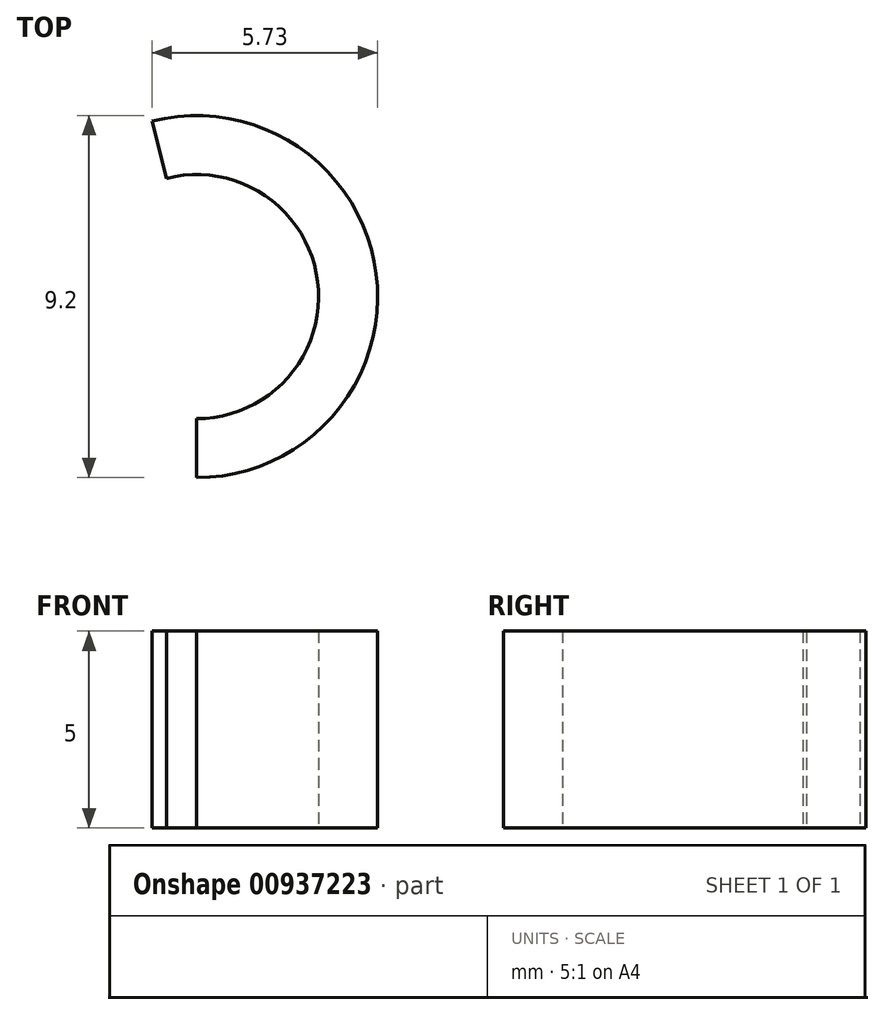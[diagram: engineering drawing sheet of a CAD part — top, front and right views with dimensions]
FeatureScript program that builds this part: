
annotation { "Feature Type Name" : "Feature", "Feature Type Description" : "" }
export const myFeature = defineFeature(function(context is Context, id is Id, definition is map)
    precondition{}
    {
        {
            var Q0;
            Q0=qCreatedBy(makeId("Top.planeOp"),FACE);
            var sketch = newSketch(context, id + "F0", { "sketchPlane" : qUnion([Q0])});
            skCircle(sketch, "E0", {"center": v(0, 0) * mm, "radius": 4.6 * mm});
            skCircle(sketch, "E1", {"center": v(0, 0) * mm, "radius": 3.1 * mm});
            skSolve(sketch);
        }
        {
            var Q0;
            Q0 = qSketchRegion(id + "F0", true);
            extrude(context, id + "F1", {"entities" : qUnion([Q0]), "depth" : 5 * mm, "offsetDistance" : 25 * mm});
        }
        {
            var Q0;
            Q0=qCreatedBy(makeId("Top.planeOp"),FACE);
            var sketch = newSketch(context, id + "F2", { "sketchPlane" : qUnion([Q0])});
            skLineSegment(sketch, "E2", {"start": v(-2.57, 10.12) * mm, "end": v(-7.73, 10.12) * mm});
            skLineSegment(sketch, "E3", {"start": v(-7.73, 10.12) * mm, "end": v(-7.73, -5.57) * mm});
            skLineSegment(sketch, "E4", {"start": v(-7.73, -5.57) * mm, "end": v(0, -5.57) * mm});
            skLineSegment(sketch, "E5", {"start": v(0, -5.57) * mm, "end": v(0, 0) * mm});
            skLineSegment(sketch, "E6", {"start": v(0, 0) * mm, "end": v(-2.57, 10.12) * mm});
            skSolve(sketch);
        }
        {
            var Q0;
            Q0 = qSketchRegion(id + "F2", true);
            extrude(context, id + "F3", {"entities" : qUnion([Q0]), "operationType" : NewBodyOperationType.REMOVE, "endBound" : BoundingType.THROUGH_ALL, "depth" : 25 * mm, "offsetDistance" : 25 * mm});
        }
    });
